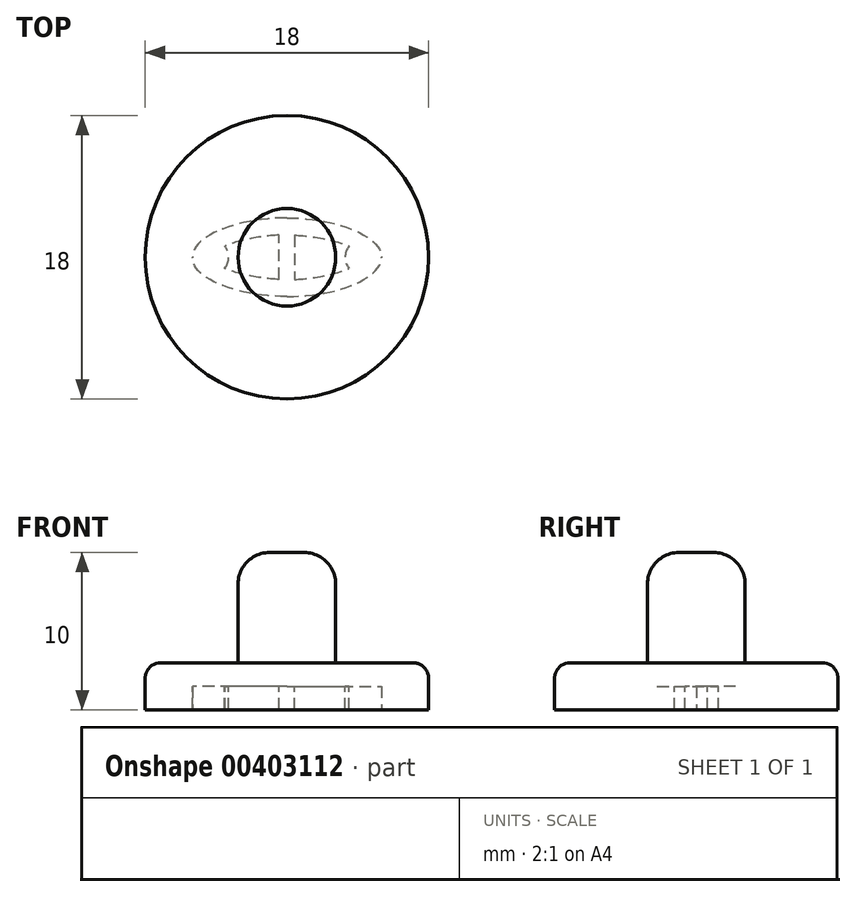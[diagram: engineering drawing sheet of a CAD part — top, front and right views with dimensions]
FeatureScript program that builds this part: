
annotation { "Feature Type Name" : "Feature", "Feature Type Description" : "" }
export const myFeature = defineFeature(function(context is Context, id is Id, definition is map)
    precondition{}
    {
        {
            var Q0;
            Q0=qCreatedBy(makeId("Top.planeOp"),FACE);
            var sketch = newSketch(context, id + "F0", { "sketchPlane" : qUnion([Q0])});
            skCircle(sketch, "E0", {"center": v(0, 0) * mm, "radius": 9 * mm});
            skLineSegment(sketch, "E1", {"start": v(0, 0) * mm, "end": v(0, 2.5) * mm});
            skLineSegment(sketch, "E2", {"start": v(0, 0) * mm, "end": v(6, 0) * mm});
            skFitSpline(sketch, "E3", {"points": [v(0, 2.5) * mm, v(6, 0) * mm], "startDerivative": vector(9.53, 0) * mm, "endDerivative": vector(-0.1, -3.98) * mm});
            skFitSpline(sketch, "E4.MirrorCS", {"points": [v(0, 2.5) * mm, v(-6, 0) * mm], "startDerivative": vector(-9.53, 0) * mm, "endDerivative": vector(0.1, -3.98) * mm});
            skFitSpline(sketch, "E5.MirrorCS", {"points": [v(0, -2.5) * mm, v(6, 0) * mm], "startDerivative": vector(9.53, 0) * mm, "endDerivative": vector(-0.1, 3.98) * mm});
            skFitSpline(sketch, "E6.MirrorCS", {"points": [v(0, -2.5) * mm, v(-6, 0) * mm], "startDerivative": vector(-9.53, 0) * mm, "endDerivative": vector(0.1, 3.98) * mm});
            skSolve(sketch);
        }
        {
            var Q0;
            Q0 = qSketchRegion(id + "F0", true);
            extrude(context, id + "F1", {"entities" : qUnion([Q0]), "depth" : 1.5 * mm});
        }
        {
            var Q0;
            Q0=makeQuery(id+"F1.opExtrude","CAP_FACE",FACE,{"disambiguationData":[OSD([sQuery(id+"F0.wireOp",EDGE,"E0"),sQuery(id+"F0.wireOp",EDGE,"E3"),sQuery(id+"F0.wireOp",EDGE,"E4.MirrorCS"),sQuery(id+"F0.wireOp",EDGE,"E5.MirrorCS"),sQuery(id+"F0.wireOp",EDGE,"E6.MirrorCS")])],"isStart":false});
            var sketch = newSketch(context, id + "F2", { "sketchPlane" : qUnion([Q0])});
            skCircle(sketch, "E7", {"center": v(0, 0) * mm, "radius": 9 * mm});
            skSolve(sketch);
        }
        {
            var Q0;
            Q0 = qSketchRegion(id + "F2", true);
            extrude(context, id + "F3", {"entities" : qUnion([Q0]), "operationType" : NewBodyOperationType.ADD, "depth" : 1.5 * mm});
        }
        {
            var Q0;
            Q0=makeQuery(id+"F3.opExtrude","CAP_EDGE",EDGE,{"disambiguationData":[OSD([sQuery(id+"F2.wireOp",EDGE,"E7")])],"isStart":false});
            fillet(context, id + "F4", {"entities" : qUnion([Q0]), "radius" : 1 * mm, "tangentPropagation" : true, "allowEdgeOverflow" : false});
        }
        {
            var Q0;
            Q0=makeQuery(id+"F3.opExtrude","CAP_FACE",FACE,{"disambiguationData":[OSD([sQuery(id+"F2.wireOp",EDGE,"E7")])],"isStart":false});
            var sketch = newSketch(context, id + "F5", { "sketchPlane" : qUnion([Q0])});
            skCircle(sketch, "E8", {"center": v(0, 0) * mm, "radius": 3.1 * mm});
            skSolve(sketch);
        }
        {
            var Q0;
            Q0 = qSketchRegion(id + "F5", true);
            extrude(context, id + "F6", {"entities" : qUnion([Q0]), "operationType" : NewBodyOperationType.ADD, "depth" : 7 * mm});
        }
        {
            var Q0;
            Q0=makeQuery(id+"F6.opExtrude","CAP_FACE",FACE,{"disambiguationData":[OSD([sQuery(id+"F5.wireOp",EDGE,"E8")])],"isStart":false});
            fillet(context, id + "F7", {"entities" : qUnion([Q0]), "radius" : 2 * mm, "tangentPropagation" : true, "allowEdgeOverflow" : false});
        }
        {
            var Q0;
            Q0=makeQuery(id+"F3.opExtrude","CAP_FACE",FACE,{"disambiguationData":[OSD([sQuery(id+"F2.wireOp",EDGE,"E7")])],"isStart":true});
            var sketch = newSketch(context, id + "F8", { "sketchPlane" : qUnion([Q0])});
            skLineSegment(sketch, "E9", {"start": v(0.5, 0) * mm, "end": v(0.5, 1.4) * mm});
            skFitSpline(sketch, "E10", {"points": [v(0.5, 1.4) * mm, v(4.7, 0) * mm], "startDerivative": vector(4.05, -0.03) * mm, "endDerivative": vector(-0.2, -2.34) * mm});
            skLineSegment(sketch, "E11.MirrorCS", {"start": v(0.5, 0) * mm, "end": v(0.5, -1.4) * mm});
            skFitSpline(sketch, "E12.MirrorCS", {"points": [v(0.5, -1.4) * mm, v(4.7, 0) * mm], "startDerivative": vector(4.05, 0.03) * mm, "endDerivative": vector(-0.2, 2.34) * mm});
            skFitSpline(sketch, "E13.MirrorCS", {"points": [v(-0.5, 1.4) * mm, v(-4.7, 0) * mm], "startDerivative": vector(-4.05, -0.03) * mm, "endDerivative": vector(0.2, -2.34) * mm});
            skFitSpline(sketch, "E14.MirrorCS", {"points": [v(-0.5, -1.4) * mm, v(-4.7, 0) * mm], "startDerivative": vector(-4.05, 0.03) * mm, "endDerivative": vector(0.2, 2.34) * mm});
            skLineSegment(sketch, "E15.MirrorCS", {"start": v(-0.5, 0) * mm, "end": v(-0.5, 1.4) * mm});
            skLineSegment(sketch, "E16.MirrorCS", {"start": v(-0.5, 0) * mm, "end": v(-0.5, -1.4) * mm});
            skArc(sketch, "E17", {"start": v(3.95, 0.7) * mm, "mid": v(3.7, 0) * mm, "end": v(3.94, -0.7) * mm});
            skArc(sketch, "E18.MirrorCS", {"start": v(-3.95, 0.7) * mm, "mid": v(-3.7, 0) * mm, "end": v(-3.94, -0.7) * mm});
            skSolve(sketch);
        }
        {
            var Q0;
            {var subQ4=sQuery(id+"F8.wireOp",EDGE,"E9");Q0=makeQuery(id+"F8.imprint","IMPRINT",FACE,{"disambiguationData":[TD([[makeQuery(id+"F8.imprint","IMPRINT",EDGE,{"derivedFrom":subQ4}),-1.0]])]});}
            var Q1;
            {var subQ0=sQuery(id+"F8.wireOp",EDGE,"E15.MirrorCS");Q1=makeQuery(id+"F8.imprint","IMPRINT",FACE,{"disambiguationData":[TD([[makeQuery(id+"F8.imprint","IMPRINT",EDGE,{"derivedFrom":subQ0}),1.0]])]});}
            var Q2;
            Q2=makeQuery(id+"F1.opExtrude","CAP_FACE",FACE,{"disambiguationData":[OSD([sQuery(id+"F0.wireOp",EDGE,"E0"),sQuery(id+"F0.wireOp",EDGE,"E3"),sQuery(id+"F0.wireOp",EDGE,"E4.MirrorCS"),sQuery(id+"F0.wireOp",EDGE,"E5.MirrorCS"),sQuery(id+"F0.wireOp",EDGE,"E6.MirrorCS")])],"isStart":true});
            extrude(context, id + "F9", {"entities" : qUnion([Q0, Q1]), "operationType" : NewBodyOperationType.ADD, "endBound" : BoundingType.UP_TO_SURFACE, "endBoundEntityFace" : qUnion([Q2]), "depth" : 25 * mm});
        }
    });
